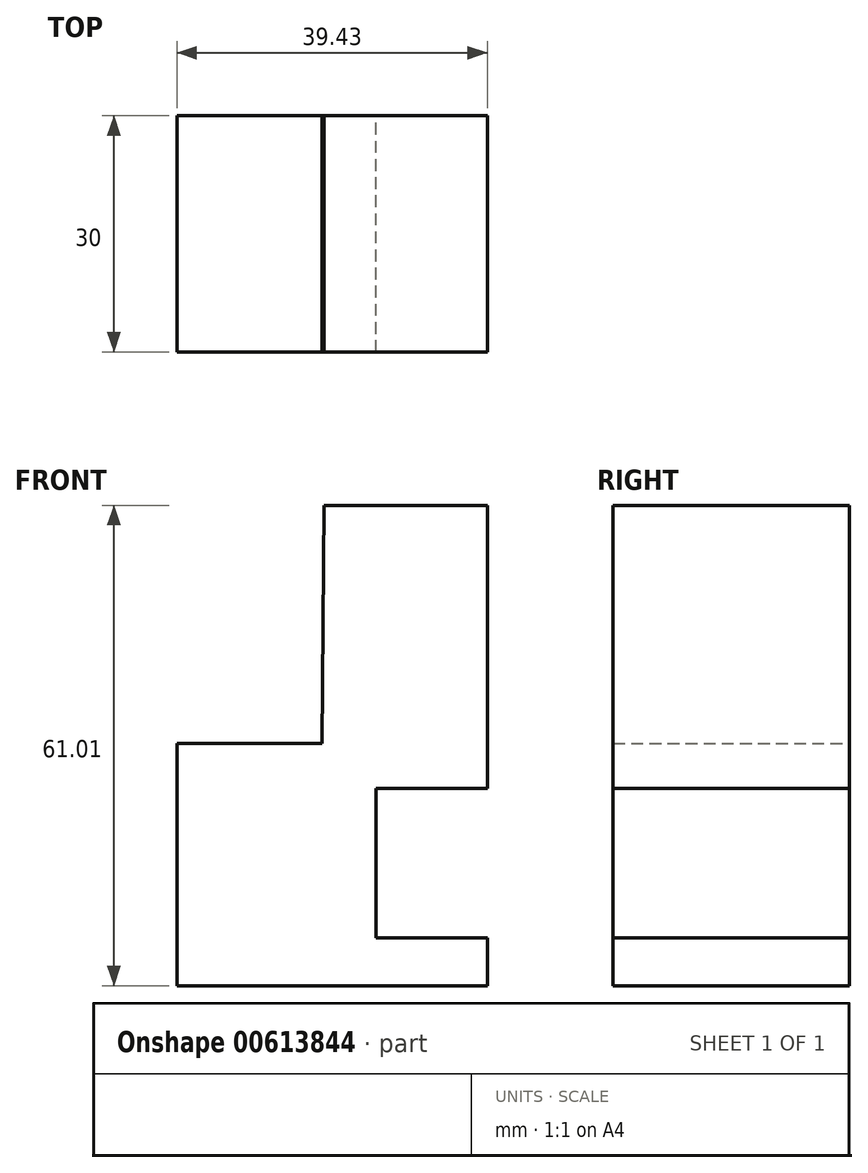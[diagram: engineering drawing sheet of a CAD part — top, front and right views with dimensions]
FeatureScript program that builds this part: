
annotation { "Feature Type Name" : "Feature", "Feature Type Description" : "" }
export const myFeature = defineFeature(function(context is Context, id is Id, definition is map)
    precondition{}
    {
        {
            var Q0;
            Q0=qCreatedBy(makeId("Front.planeOp"),FACE);
            var sketch = newSketch(context, id + "F0", { "sketchPlane" : qUnion([Q0])});
            skLineSegment(sketch, "E0", {"start": v(-36.12, 45.04) * mm, "end": v(-15.4, 45.04) * mm});
            skLineSegment(sketch, "E1", {"start": v(-15.4, 45.04) * mm, "end": v(-15.4, 9.07) * mm});
            skLineSegment(sketch, "E2", {"start": v(-15.4, 9.07) * mm, "end": v(-29.5, 9.07) * mm});
            skLineSegment(sketch, "E3", {"start": v(-29.5, 9.07) * mm, "end": v(-29.5, -9.93) * mm});
            skLineSegment(sketch, "E4", {"start": v(-29.5, -9.93) * mm, "end": v(-15.4, -9.93) * mm});
            skLineSegment(sketch, "E5", {"start": v(-15.4, -9.93) * mm, "end": v(-15.4, -15.97) * mm});
            skLineSegment(sketch, "E6", {"start": v(-15.4, -15.97) * mm, "end": v(-54.83, -15.97) * mm});
            skLineSegment(sketch, "E7", {"start": v(-54.83, -15.97) * mm, "end": v(-54.83, 14.82) * mm});
            skLineSegment(sketch, "E8", {"start": v(-54.83, 14.82) * mm, "end": v(-36.4, 14.82) * mm});
            skLineSegment(sketch, "E9", {"start": v(-36.4, 14.82) * mm, "end": v(-36.12, 45.04) * mm});
            skSolve(sketch);
        }
        {
            var Q0;
            Q0 = qSketchRegion(id + "F0", true);
            extrude(context, id + "F1", {"entities" : qUnion([Q0]), "depth" : 30 * mm, "offsetDistance" : 25 * mm});
        }
    });
